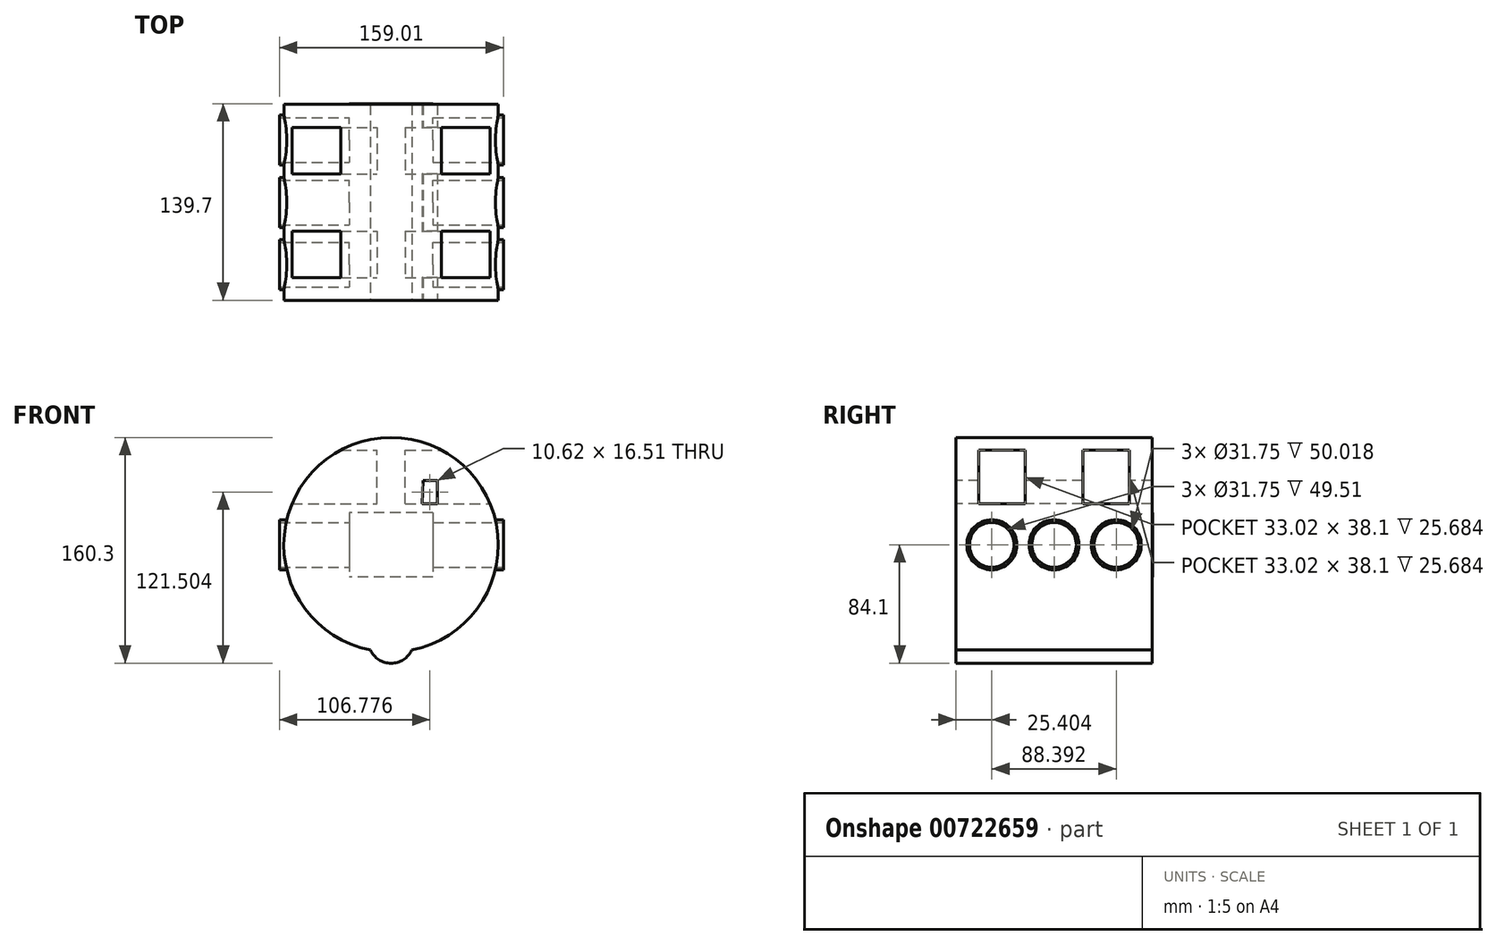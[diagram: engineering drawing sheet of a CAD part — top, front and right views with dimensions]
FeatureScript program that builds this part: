
annotation { "Feature Type Name" : "Feature", "Feature Type Description" : "" }
export const myFeature = defineFeature(function(context is Context, id is Id, definition is map)
    precondition{}
    {
        {
            var Q0;
            Q0=qCreatedBy(makeId("Front.planeOp"),FACE);
            var sketch = newSketch(context, id + "F0", { "sketchPlane" : qUnion([Q0])});
            skCircle(sketch, "E0", {"center": v(0, 0) * mm, "radius": 76.2 * mm});
            skSolve(sketch);
        }
        {
            var Q0;
            Q0=makeQuery(id+"F0.imprint","IMPRINT",FACE,{"disambiguationData":[TD([[makeQuery(id+"F0.imprint","IMPRINT",EDGE,{"derivedFrom":sQuery(id+"F0.wireOp",EDGE,"E0")}),1.0]])]});
            extrude(context, id + "F1", {"entities" : qUnion([Q0]), "endBound" : BoundingType.SYMMETRIC, "depth" : 139.2 * mm, "offsetDistance" : 25.4 * mm});
        }
        {
            var Q0;
            Q0=qCreatedBy(makeId("Right.planeOp"),FACE);
            cPlane(context, id + "F2", {"entities" : qUnion([Q0]), "cplaneType" : CPlaneType.OFFSET, "offset" : 79.76 * mm, "width" : 152.4 * mm, "height" : 152.4 * mm});
        }
        {
            var Q0;
            Q0=qCreatedBy(id+"F2.planeOp",FACE);
            var sketch = newSketch(context, id + "F3", { "sketchPlane" : qUnion([Q0])});
            skCircle(sketch, "E1", {"center": v(0, 0) * mm, "radius": 17.78 * mm});
            skCircle(sketch, "E2", {"center": v(-44.2, 0) * mm, "radius": 17.78 * mm});
            skCircle(sketch, "E3", {"center": v(44.2, 0) * mm, "radius": 17.78 * mm});
            skSolve(sketch);
        }
        {
            var Q0;
            Q0=makeQuery(id+"F3.imprint","IMPRINT",FACE,{"disambiguationData":[TD([[makeQuery(id+"F3.imprint","IMPRINT",EDGE,{"derivedFrom":sQuery(id+"F3.wireOp",EDGE,"E2")}),1.0]])]});
            var Q1;
            Q1=makeQuery(id+"F3.imprint","IMPRINT",FACE,{"disambiguationData":[TD([[makeQuery(id+"F3.imprint","IMPRINT",EDGE,{"derivedFrom":sQuery(id+"F3.wireOp",EDGE,"E1")}),1.0]])]});
            var Q2;
            Q2=makeQuery(id+"F3.imprint","IMPRINT",FACE,{"disambiguationData":[TD([[makeQuery(id+"F3.imprint","IMPRINT",EDGE,{"derivedFrom":sQuery(id+"F3.wireOp",EDGE,"E3")}),1.0]])]});
            extrude(context, id + "F4", {"entities" : qUnion([Q0, Q1, Q2]), "operationType" : NewBodyOperationType.ADD, "oppositeDirection" : true, "depth" : 159 * mm, "offsetDistance" : 25.4 * mm});
        }
        {
            var Q0;
            Q0=qCreatedBy(id+"F2.planeOp",FACE);
            var sketch = newSketch(context, id + "F5", { "sketchPlane" : qUnion([Q0])});
            skCircle(sketch, "E4", {"center": v(0, 0) * mm, "radius": 15.88 * mm});
            skCircle(sketch, "E5", {"center": v(-44.2, 0) * mm, "radius": 15.88 * mm});
            skCircle(sketch, "E6", {"center": v(44.2, 0) * mm, "radius": 15.88 * mm});
            skSolve(sketch);
        }
        {
            var Q0;
            Q0=makeQuery(id+"F5.imprint","IMPRINT",FACE,{"disambiguationData":[TD([[makeQuery(id+"F5.imprint","IMPRINT",EDGE,{"derivedFrom":sQuery(id+"F5.wireOp",EDGE,"E5")}),1.0]])]});
            var Q1;
            Q1=makeQuery(id+"F5.imprint","IMPRINT",FACE,{"disambiguationData":[TD([[makeQuery(id+"F5.imprint","IMPRINT",EDGE,{"derivedFrom":sQuery(id+"F5.wireOp",EDGE,"E4")}),1.0]])]});
            var Q2;
            Q2=makeQuery(id+"F5.imprint","IMPRINT",FACE,{"disambiguationData":[TD([[makeQuery(id+"F5.imprint","IMPRINT",EDGE,{"derivedFrom":sQuery(id+"F5.wireOp",EDGE,"E6")}),1.0]])]});
            extrude(context, id + "F6", {"entities" : qUnion([Q0, Q1, Q2]), "operationType" : NewBodyOperationType.REMOVE, "oppositeDirection" : true, "depth" : 258.06 * mm, "offsetDistance" : 25.4 * mm});
        }
        {
            var Q0;
            Q0=makeQuery(id+"F1.opExtrude","CAP_FACE",FACE,{"disambiguationData":[OSD([sQuery(id+"F0.wireOp",EDGE,"E0")])],"isStart":false});
            var sketch = newSketch(context, id + "F7", { "sketchPlane" : qUnion([Q0])});
            skLineSegment(sketch, "E7.bottom", {"start": v(29.74, 22.88) * mm, "end": v(-29.74, 22.88) * mm});
            skLineSegment(sketch, "E7.top", {"start": v(29.74, -22.88) * mm, "end": v(-29.74, -22.88) * mm});
            skLineSegment(sketch, "E7.left", {"start": v(29.74, 22.88) * mm, "end": v(29.74, -22.88) * mm});
            skLineSegment(sketch, "E7.right", {"start": v(-29.74, 22.88) * mm, "end": v(-29.74, -22.88) * mm});
            skPoint(sketch, "E7.middle", {"position": v(0, 0) * mm});
            skSolve(sketch);
        }
        {
            var Q0;
            Q0=makeQuery(id+"F7.imprint","IMPRINT",FACE,{"disambiguationData":[TD([[makeQuery(id+"F7.imprint","IMPRINT",EDGE,{"derivedFrom":sQuery(id+"F7.wireOp",EDGE,"E7.bottom")}),1.0]])]});
            extrude(context, id + "F8", {"entities" : qUnion([Q0]), "operationType" : NewBodyOperationType.ADD, "oppositeDirection" : true, "depth" : 139.7 * mm, "offsetDistance" : 25.4 * mm});
        }
        {
            var Q0;
            Q0=qCreatedBy(id+"F2.planeOp",FACE);
            var sketch = newSketch(context, id + "F9", { "sketchPlane" : qUnion([Q0])});
            skLineSegment(sketch, "E8", {"start": v(0, 65.02) * mm, "end": v(0, 36.36) * mm});
            skLineSegment(sketch, "E9.bottom", {"start": v(-53.34, 67.25) * mm, "end": v(-20.32, 67.25) * mm});
            skLineSegment(sketch, "E9.top", {"start": v(-53.34, 29.15) * mm, "end": v(-20.32, 29.15) * mm});
            skLineSegment(sketch, "E9.left", {"start": v(-53.34, 67.25) * mm, "end": v(-53.34, 29.15) * mm});
            skLineSegment(sketch, "E9.right", {"start": v(-20.32, 67.25) * mm, "end": v(-20.32, 29.15) * mm});
            skPoint(sketch, "E9.middle", {"position": v(-36.83, 48.2) * mm});
            skLineSegment(sketch, "E10.bottom", {"start": v(20.32, 67.25) * mm, "end": v(53.34, 67.25) * mm});
            skLineSegment(sketch, "E10.top", {"start": v(20.32, 29.15) * mm, "end": v(53.34, 29.15) * mm});
            skLineSegment(sketch, "E10.left", {"start": v(20.32, 67.25) * mm, "end": v(20.32, 29.15) * mm});
            skLineSegment(sketch, "E10.right", {"start": v(53.34, 67.25) * mm, "end": v(53.34, 29.15) * mm});
            skPoint(sketch, "E10.middle", {"position": v(36.83, 48.2) * mm});
            skSolve(sketch);
        }
        {
            var Q0;
            Q0=makeQuery(id+"F9.imprint","IMPRINT",FACE,{"disambiguationData":[TD([[makeQuery(id+"F9.imprint","IMPRINT",EDGE,{"derivedFrom":sQuery(id+"F9.wireOp",EDGE,"E9.bottom")}),-1.0]])]});
            var Q1;
            Q1=makeQuery(id+"F9.imprint","IMPRINT",FACE,{"disambiguationData":[TD([[makeQuery(id+"F9.imprint","IMPRINT",EDGE,{"derivedFrom":sQuery(id+"F9.wireOp",EDGE,"E10.bottom")}),-1.0]])]});
            extrude(context, id + "F10", {"entities" : qUnion([Q0, Q1]), "operationType" : NewBodyOperationType.REMOVE, "oppositeDirection" : true, "depth" : 170.43 * mm, "offsetDistance" : 25.4 * mm});
        }
        {
            var Q0;
            Q0=makeQuery(id+"F1.opExtrude","CAP_FACE",FACE,{"disambiguationData":[OSD([sQuery(id+"F0.wireOp",EDGE,"E0")])],"isStart":true});
            var sketch = newSketch(context, id + "F11", { "sketchPlane" : qUnion([Q0])});
            skLineSegment(sketch, "E11.bottom", {"start": v(-10.15, 75.52) * mm, "end": v(10.15, 75.52) * mm});
            skLineSegment(sketch, "E11.top", {"start": v(-10.15, 13.3) * mm, "end": v(10.15, 13.3) * mm});
            skLineSegment(sketch, "E11.left", {"start": v(-10.15, 75.52) * mm, "end": v(-10.15, 13.3) * mm});
            skLineSegment(sketch, "E11.right", {"start": v(10.15, 75.52) * mm, "end": v(10.15, 13.3) * mm});
            skPoint(sketch, "E11.middle", {"position": v(0, 44.4) * mm});
            skSolve(sketch);
        }
        {
            var Q0;
            {var subQ0=sQuery(id+"F11.wireOp",EDGE,"E11.bottom");Q0=makeQuery(id+"F11.imprint","IMPRINT",FACE,{"disambiguationData":[TD([[makeQuery(id+"F11.imprint","IMPRINT",EDGE,{"derivedFrom":subQ0}),-1.0]])]});}
            extrude(context, id + "F12", {"entities" : qUnion([Q0]), "operationType" : NewBodyOperationType.ADD, "oppositeDirection" : true, "depth" : 135.13 * mm, "offsetDistance" : 25.4 * mm});
        }
        {
            var Q0;
            Q0=qCreatedBy(makeId("Front.planeOp"),FACE);
            var sketch = newSketch(context, id + "F13", { "sketchPlane" : qUnion([Q0])});
            skCircle(sketch, "E12", {"center": v(0, -67.74) * mm, "radius": 16.35 * mm});
            skSolve(sketch);
        }
        {
            var Q0;
            Q0=makeQuery(id+"F13.imprint","IMPRINT",FACE,{"disambiguationData":[TD([[makeQuery(id+"F13.imprint","IMPRINT",EDGE,{"derivedFrom":sQuery(id+"F13.wireOp",EDGE,"E12")}),1.0]])]});
            extrude(context, id + "F14", {"entities" : qUnion([Q0]), "operationType" : NewBodyOperationType.ADD, "endBound" : BoundingType.SYMMETRIC, "oppositeDirection" : true, "depth" : 139.2 * mm, "offsetDistance" : 25.4 * mm});
        }
        {
            var Q0;
            Q0=makeQuery(id+"F12.boolean.opBoolean","SPLIT",FACE,{"disambiguationData":[TD([makeQuery(id+"F12.opExtrude","SWEPT_FACE",FACE,{"disambiguationData":[OSD([sQuery(id+"F11.wireOp",EDGE,"E11.left")])]})])],"derivedFrom":makeQuery(id+"F10.boolean.opBoolean","COPY",FACE,{"derivedFrom":makeQuery(id+"F10.opExtrude","SWEPT_FACE",FACE,{"disambiguationData":[OSD([sQuery(id+"F9.wireOp",EDGE,"E9.left")])]})})});
            var sketch = newSketch(context, id + "F15", { "sketchPlane" : qUnion([Q0])});
            skLineSegment(sketch, "E13", {"start": v(-32.84, 29.15) * mm, "end": v(-32.84, 45.66) * mm});
            skLineSegment(sketch, "E14", {"start": v(-32.84, 45.66) * mm, "end": v(-22.68, 45.66) * mm});
            skLineSegment(sketch, "E15", {"start": v(-22.68, 45.66) * mm, "end": v(-22.22, 29.15) * mm});
            skLineSegment(sketch, "E16", {"start": v(-22.22, 29.15) * mm, "end": v(-32.84, 29.15) * mm});
            skSolve(sketch);
        }
        {
            var Q0;
            Q0=makeQuery(id+"F15.imprint","IMPRINT",FACE,{"disambiguationData":[TD([[makeQuery(id+"F15.imprint","IMPRINT",EDGE,{"derivedFrom":sQuery(id+"F15.wireOp",EDGE,"E13")}),-1.0]])]});
            extrude(context, id + "F16", {"entities" : qUnion([Q0]), "operationType" : NewBodyOperationType.REMOVE, "endBound" : BoundingType.SYMMETRIC, "depth" : 273.3 * mm, "offsetDistance" : 25.4 * mm});
        }
    });
